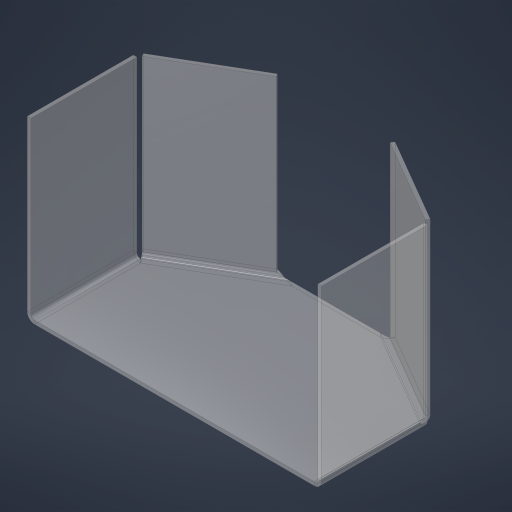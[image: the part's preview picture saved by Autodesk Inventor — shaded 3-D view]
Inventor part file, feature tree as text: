
AUTODESK INVENTOR PART (.ipt)
format: ipt  version: 2023.4 (Build 274418000, 418)  size: 230,400 bytes
history: native  units: in
note: dims shown in document units (in); Inventor stores cm internally (conversion verified against a paired STEP export)
features: sheet_metal_op x4, sketch x2, other x2
ambient origin geometry x8: Origin, YZ Plane, XZ Plane, XY Plane, X Axis, Y Axis, Z Axis, Center Point
bodies: Solid1 (feature_tree)
feature tree (8):
  sheet_metal_op  "Face1"
  sheet_metal_op  "Flange1"
  sketch  "Sketch1"  dims[d0=10.0in]
  other  "Plate1"
  sketch  "Sketch2"  dims[d1=5.5in d2=0.125in d3=4.0in d4=3.75in d5=0.125in d6=0.0625in d7=0.25in d8=0.125in d9=6.0in d10=90.0deg d11=0.125in d12=0.5in d13=0.125in d14=0.125in]
  other  "Plate2"
  sheet_metal_op  "Bend1"
  sheet_metal_op  "Corner1"
